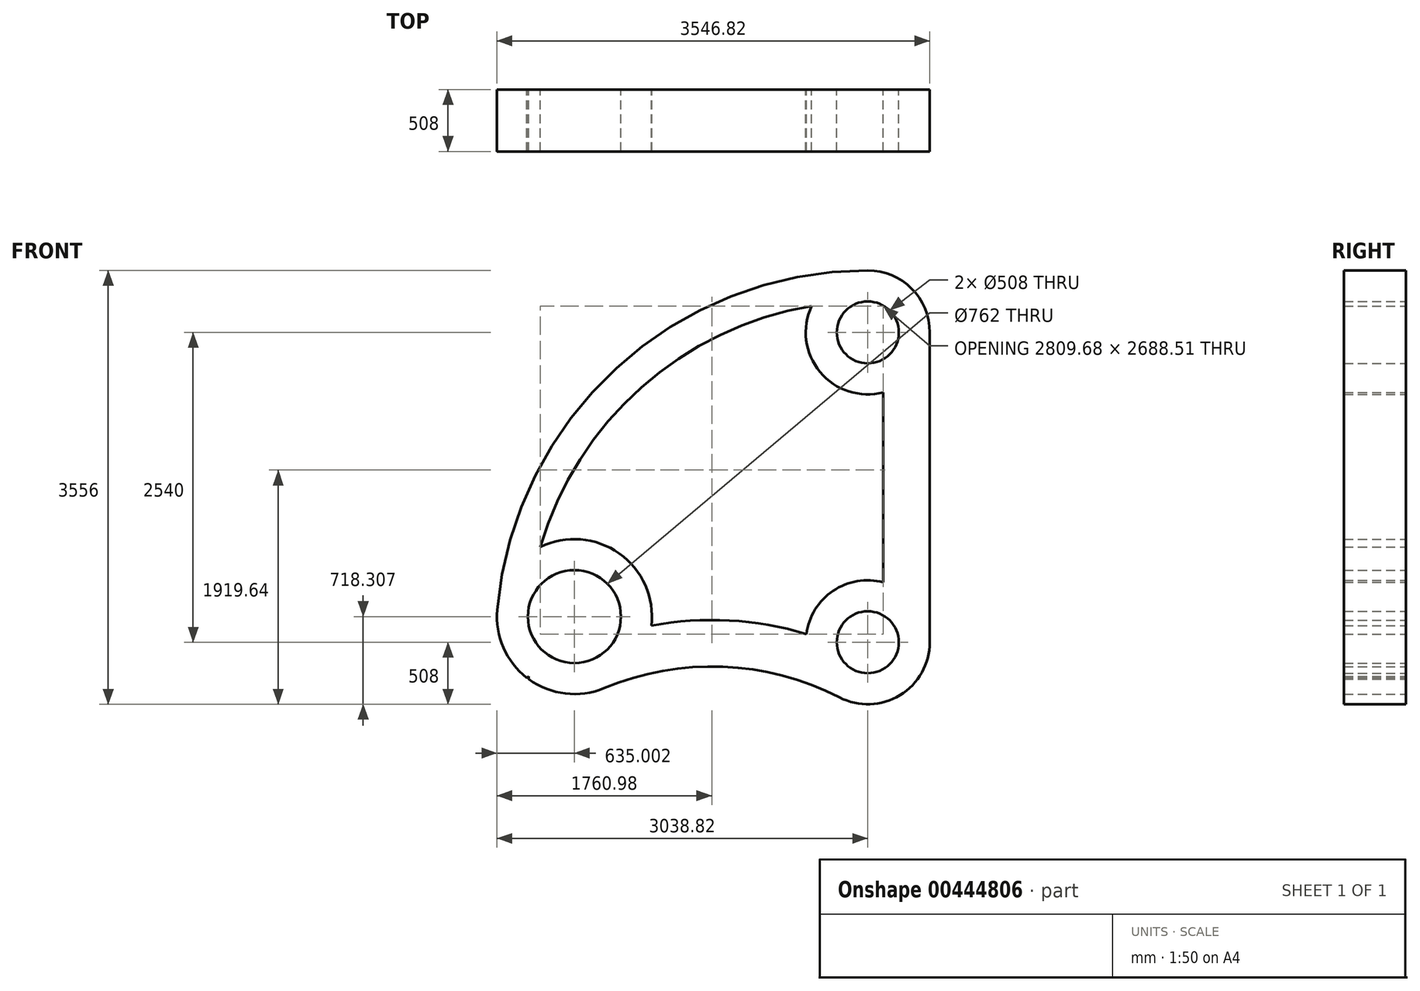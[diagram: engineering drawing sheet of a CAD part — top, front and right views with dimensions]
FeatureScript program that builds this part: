
annotation { "Feature Type Name" : "Feature", "Feature Type Description" : "" }
export const myFeature = defineFeature(function(context is Context, id is Id, definition is map)
    precondition{}
    {
        {
            var Q0;
            Q0=qCreatedBy(makeId("Front.planeOp"),FACE);
            var sketch = newSketch(context, id + "F0", { "sketchPlane" : qUnion([Q0])});
            skCircle(sketch, "E0", {"center": v(0, 0) * mm, "radius": 254 * mm});
            skArc(sketch, "E1", {"start": v(-232.28, -451.79) * mm, "mid": v(264.64, -433.63) * mm, "end": v(508, 0) * mm});
            skCircle(sketch, "E2", {"center": v(0, 2540) * mm, "radius": 254 * mm});
            skArc(sketch, "E3", {"start": v(508, 2540) * mm, "mid": v(359.21, 2899.21) * mm, "end": v(0, 3048) * mm});
            skLineSegment(sketch, "E4", {"start": v(508, 0) * mm, "end": v(508, 2540) * mm});
            skArc(sketch, "E5", {"start": v(0, 3048) * mm, "mid": v(-2059.2, 2247.22) * mm, "end": v(-3036.4, 265.65) * mm});
            skCircle(sketch, "E6", {"center": v(-2403.82, 210.3) * mm, "radius": 381 * mm});
            skArc(sketch, "E7", {"start": v(-3036.4, 265.65) * mm, "mid": v(-2778.5, -302.37) * mm, "end": v(-2158.97, -375.6) * mm});
            skArc(sketch, "E8", {"start": v(-232.28, -451.79) * mm, "mid": v(-1187.2, -200.6) * mm, "end": v(-2158.97, -375.6) * mm});
            skLineSegment(sketch, "E9.0", {"start": v(127, 491.87) * mm, "end": v(127, 2048.13) * mm});
            skArc(sketch, "E10.0", {"start": v(-459.84, 2755.9) * mm, "mid": v(-1855.83, 2088.62) * mm, "end": v(-2682.68, 780.8) * mm});
            skArc(sketch, "E11.trimOffspring", {"start": v(-2779.82, -281.18) * mm, "mid": v(-2778.69, -292.14) * mm, "end": v(-2777.51, -303.1) * mm});
            skArc(sketch, "E12.trimOffspring", {"start": v(-2779.82, -281.18) * mm, "mid": v(-2786.83, -285.98) * mm, "end": v(-2793.83, -290.8) * mm});
            skArc(sketch, "E13.trimOffspring", {"start": v(-503.51, 67.39) * mm, "mid": v(-1134.23, 178.32) * mm, "end": v(-1773.21, 135.7) * mm});
            skLineSegment(sketch, "E14.trimOffspring", {"start": v(-1699.09, 148.65) * mm, "end": v(-1771.23, 154.96) * mm});
            skArc(sketch, "E15.trimOffspring", {"start": v(-1773.21, 135.7) * mm, "mid": v(-2036.44, 728.25) * mm, "end": v(-2682.68, 780.8) * mm});
            skArc(sketch, "E16.trimOffspring", {"start": v(127, 491.87) * mm, "mid": v(-283.7, 421.4) * mm, "end": v(-503.51, 67.39) * mm});
            skArc(sketch, "E17.trimOffspring", {"start": v(-459.84, 2755.9) * mm, "mid": v(-391.06, 2215.76) * mm, "end": v(127, 2048.13) * mm});
            skSolve(sketch);
        }
        {
            var Q0;
            Q0=makeQuery(id+"F0.imprint","IMPRINT",FACE,{"disambiguationData":[TD([[makeQuery(id+"F0.imprint","IMPRINT",EDGE,{"derivedFrom":sQuery(id+"F0.wireOp",EDGE,"E0")}),-1.0]])]});
            extrude(context, id + "F1", {"entities" : qUnion([Q0]), "depth" : 508 * mm});
        }
    });
